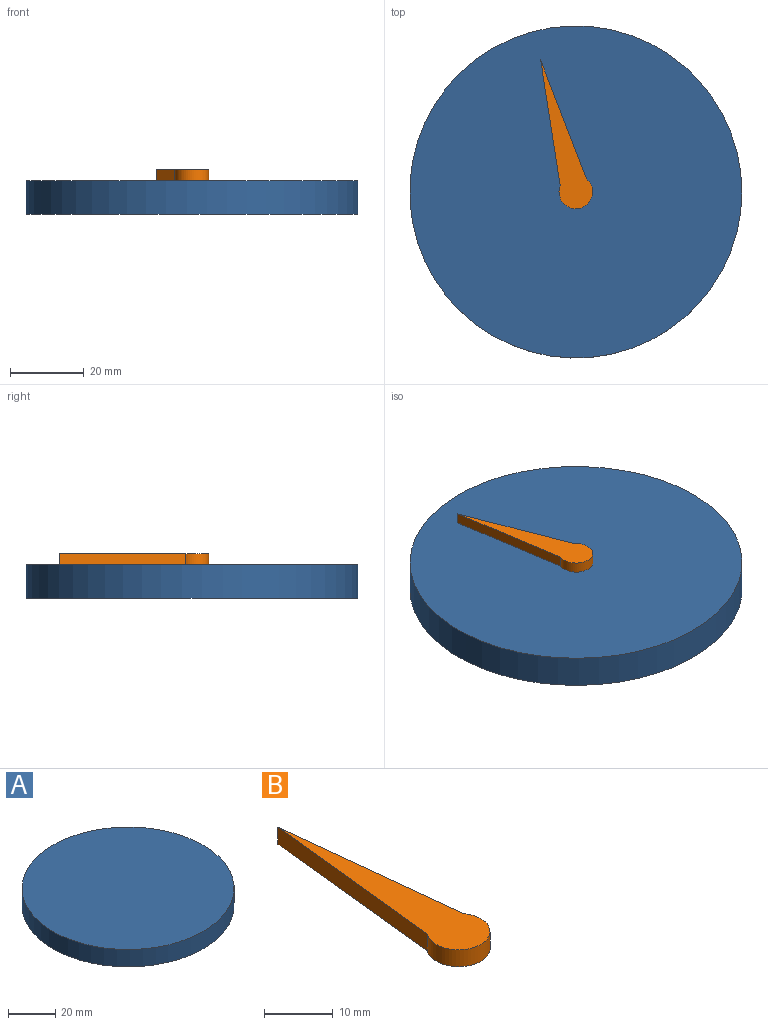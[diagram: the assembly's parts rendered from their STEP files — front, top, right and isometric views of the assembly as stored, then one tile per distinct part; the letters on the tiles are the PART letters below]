
ASSEMBLY  parts=2 mates=1
PART A: 3 faces, bbox 90x90x9 mm
  f0: cylinder r=44.98mm len=89.96mm, axis (0,0,-1), area 2543.5mm2, adj f1,f2
  f1: plane 89.96x89.96mm, normal (0,0,1), area 6355.9mm2, adj f0
  f2: plane 89.96x89.96mm, normal (0,0,-1), area 6355.9mm2, adj f0
PART B: 5 faces, bbox 9.1x41.6x3 mm
  f0: cylinder r=4.56mm len=9.13mm, axis (0,0,-1), area 60.4mm2, adj f1,f2,f3,f4
  f1: plane 34.32x3.68mm, normal (0.99,0.11,0), area 103.6mm2, adj f0,f2,f3,f4
  f2: plane 34.29x3.66mm, normal (-0.99,0.11,0), area 103.5mm2, adj f0,f1,f3,f4
  f3: plane 41.58x9.13mm, normal (0,0,1), area 181.8mm2, adj f0,f1,f2
  f4: plane 41.58x9.13mm, normal (0,0,-1), area 181.8mm2, adj f0,f1,f2
PLACE A at identity fixed
PLACE B rot(axis=(0,0,1),14.9deg) t=(0,0,0)mm
MATE revolute A.f0 <-> B.f0  axis (0,0,1) through (0,0,9)mm
